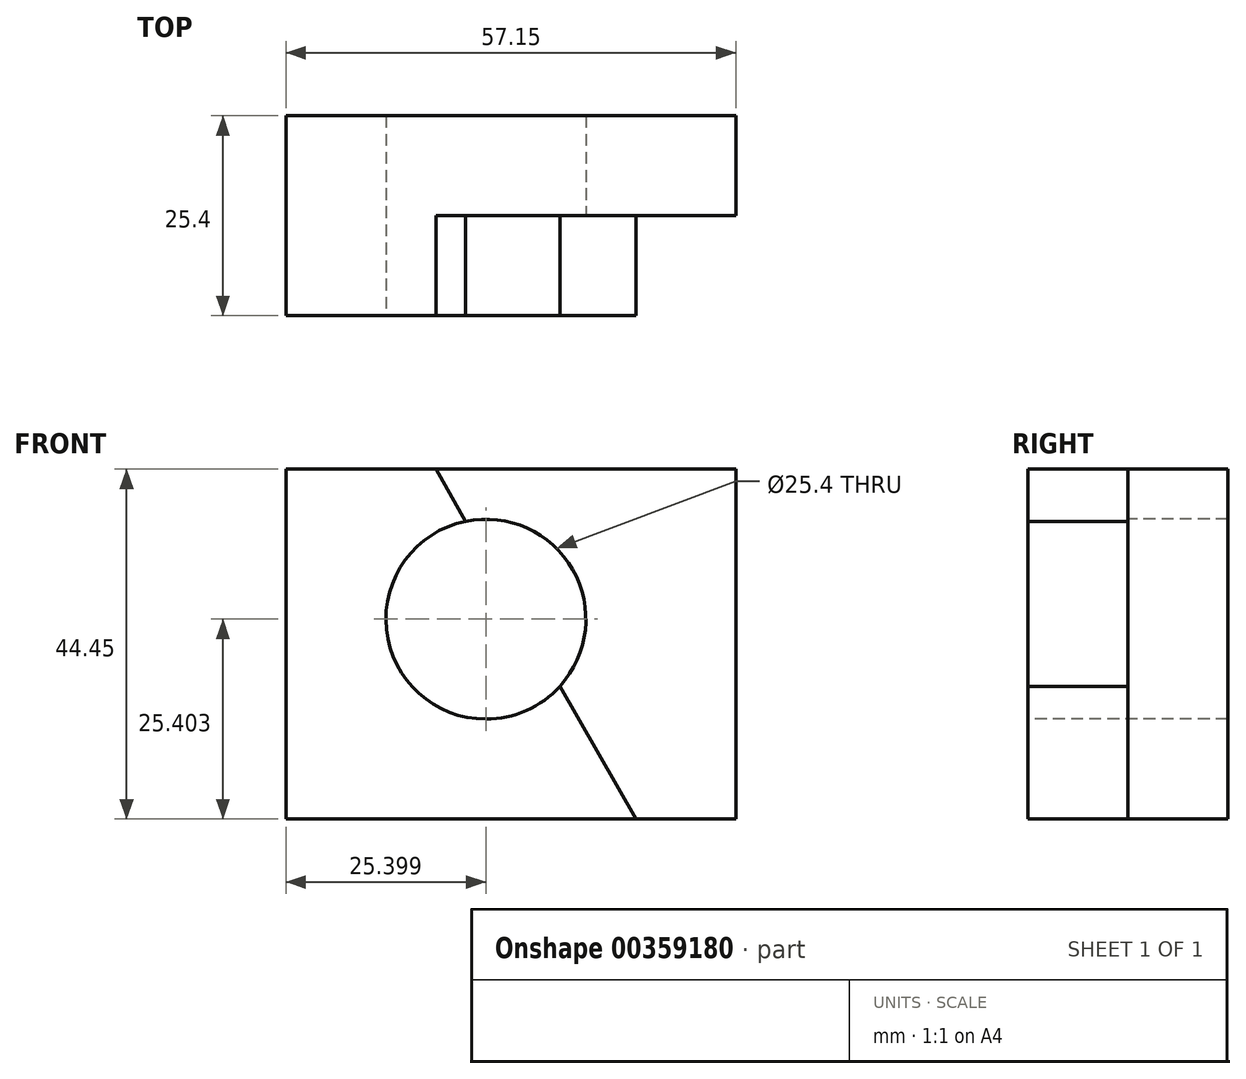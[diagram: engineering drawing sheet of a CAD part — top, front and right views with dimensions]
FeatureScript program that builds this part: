
annotation { "Feature Type Name" : "Feature", "Feature Type Description" : "" }
export const myFeature = defineFeature(function(context is Context, id is Id, definition is map)
    precondition{}
    {
        {
            var Q0;
            Q0=qCreatedBy(makeId("Front.planeOp"),FACE);
            var sketch = newSketch(context, id + "F0", { "sketchPlane" : qUnion([Q0])});
            skLineSegment(sketch, "E0.bottom", {"start": v(-45.86, 23.77) * mm, "end": v(11.29, 23.77) * mm});
            skLineSegment(sketch, "E0.top", {"start": v(-45.86, -20.68) * mm, "end": v(11.29, -20.68) * mm});
            skLineSegment(sketch, "E0.left", {"start": v(-45.86, 23.77) * mm, "end": v(-45.86, -20.68) * mm});
            skLineSegment(sketch, "E0.right", {"start": v(11.29, 23.77) * mm, "end": v(11.29, -20.68) * mm});
            skSolve(sketch);
        }
        {
            var Q0;
            Q0 = qSketchRegion(id + "F0", true);
            extrude(context, id + "F1", {"entities" : qUnion([Q0]), "depth" : 25.4 * mm});
        }
        {
            var Q0;
            Q0=makeQuery(id+"F1.opExtrude","CAP_FACE",FACE,{"disambiguationData":[OSD([sQuery(id+"F0.wireOp",EDGE,"E0.bottom"),sQuery(id+"F0.wireOp",EDGE,"E0.top"),sQuery(id+"F0.wireOp",EDGE,"E0.left"),sQuery(id+"F0.wireOp",EDGE,"E0.right")])],"isStart":false});
            var sketch = newSketch(context, id + "F2", { "sketchPlane" : qUnion([Q0])});
            skCircle(sketch, "E1", {"center": v(-20.46, 4.72) * mm, "radius": 12.7 * mm});
            skSolve(sketch);
        }
        {
            var Q0;
            Q0=makeQuery(id+"F2.imprint","IMPRINT",FACE,{"disambiguationData":[TD([[makeQuery(id+"F2.imprint","IMPRINT",EDGE,{"derivedFrom":sQuery(id+"F2.wireOp",EDGE,"E1")}),1.0]])]});
            extrude(context, id + "F3", {"entities" : qUnion([Q0]), "operationType" : NewBodyOperationType.REMOVE, "oppositeDirection" : true, "depth" : 25.4 * mm});
        }
        {
            var Q0;
            Q0=makeQuery(id+"F1.opExtrude","CAP_FACE",FACE,{"disambiguationData":[OSD([sQuery(id+"F0.wireOp",EDGE,"E0.bottom"),sQuery(id+"F0.wireOp",EDGE,"E0.top"),sQuery(id+"F0.wireOp",EDGE,"E0.left"),sQuery(id+"F0.wireOp",EDGE,"E0.right")])],"isStart":false});
            var sketch = newSketch(context, id + "F4", { "sketchPlane" : qUnion([Q0])});
            skLineSegment(sketch, "E2", {"start": v(-26.81, 23.77) * mm, "end": v(-1.41, -20.68) * mm});
            skSolve(sketch);
        }
        {
            var Q0;
            {var subQ0=makeQuery(id+"F1.opExtrude","CAP_EDGE",EDGE,{"disambiguationData":[OSD([sQuery(id+"F0.wireOp",EDGE,"E0.right")])],"isStart":false});Q0=makeQuery(id+"F4.imprint","IMPRINT",FACE,{"disambiguationData":[TD([[makeQuery(id+"F4.imprint","IMPRINT",EDGE,{"derivedFrom":subQ0}),-1.0]])]});}
            extrude(context, id + "F5", {"entities" : qUnion([Q0]), "operationType" : NewBodyOperationType.REMOVE, "oppositeDirection" : true, "depth" : 12.7 * mm});
        }
    });
